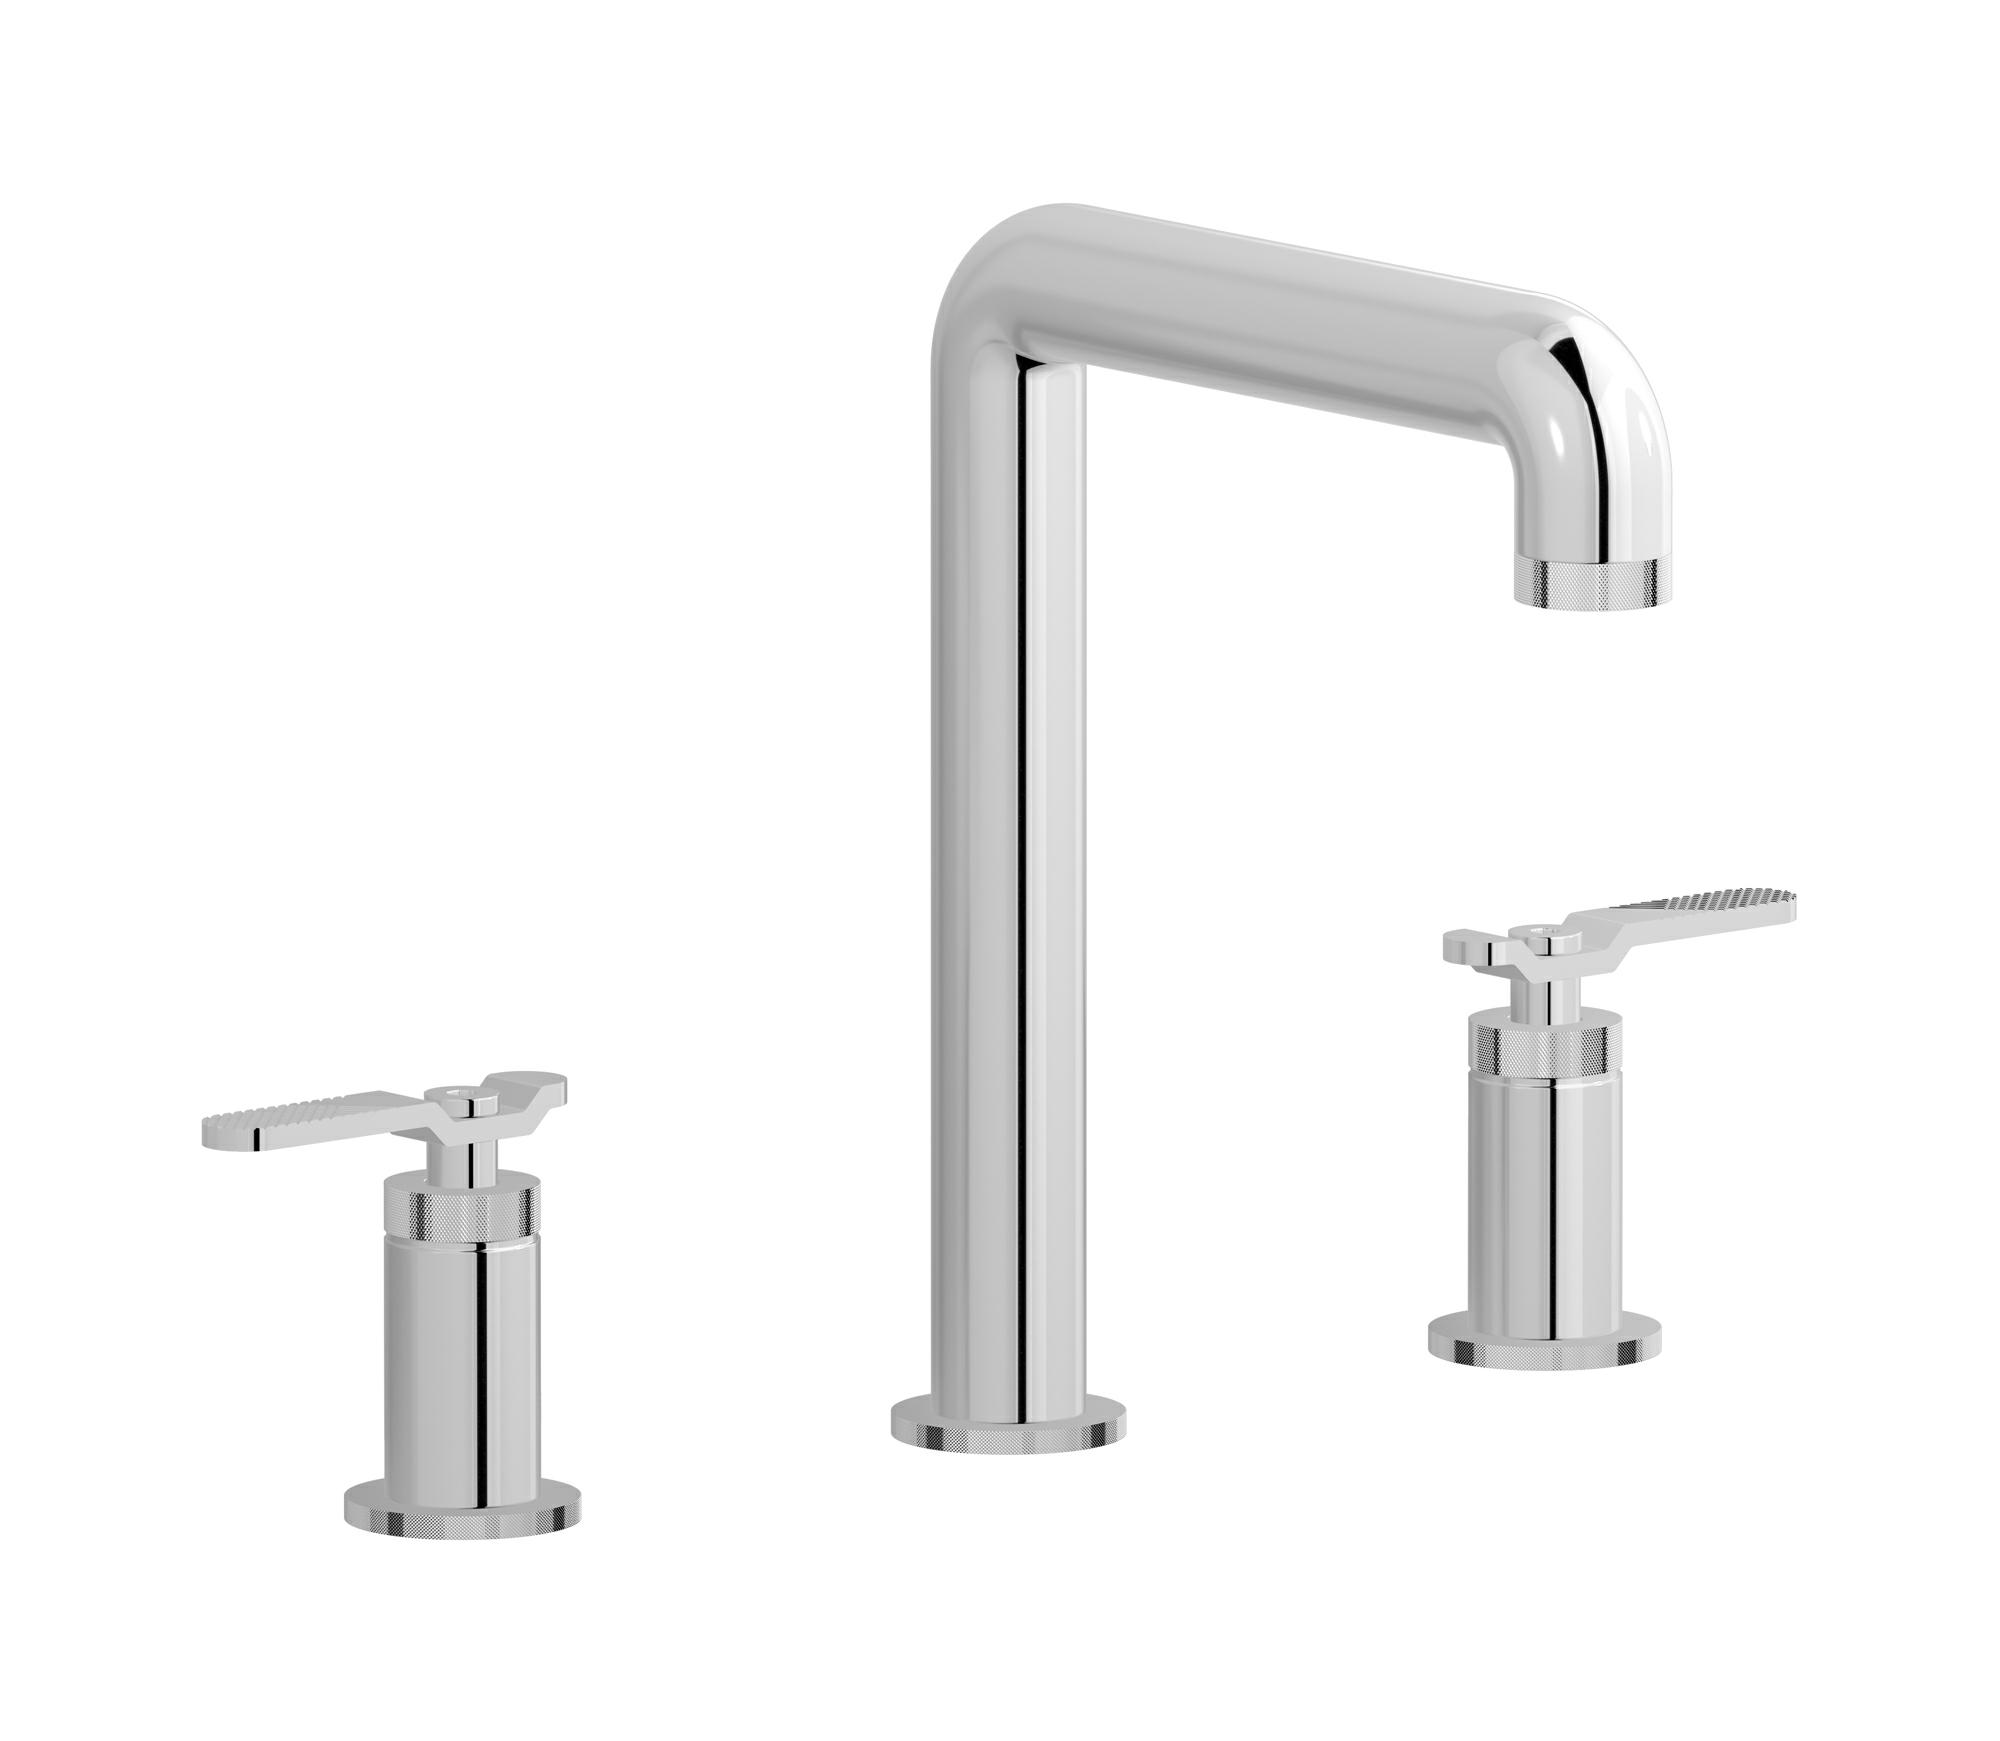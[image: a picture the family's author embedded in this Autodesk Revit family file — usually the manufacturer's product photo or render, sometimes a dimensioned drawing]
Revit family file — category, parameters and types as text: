
# Revit family: B2390
name_source: partatom
category: Apparecchi idraulici
units: mm (PartAtom-declared; Revit-internal decimal feet)

## family parameters
Basato su piano di lavoro = No
Condiviso = No
Mantieni orientamento annotazione = No
Numero OmniClass = 23.45.55.17
Punto di calcolo locali = No
Quota connettore circolare = Usa diametro
Sempre verticale = Sì
Taglio con vuoti quando caricato = No
Tipo di parte = Normale
Titolo OmniClass = Mixing Faucets

## types (13) — shared parameters
Cold water inlet = 10 mm  [stored 0.0328084 ft]
Commenti sul tipo = Three holes washbasin set with tall spout
Connessione CW = No
Connessione HW = No
Connessione di scarico = No
Connessione di ventilazione = No
Descrizione = Three holes washbasin set with tall spout
Hot water inlet = 10 mm  [stored 0.0328084 ft]
Produttore = IB Rubinetterie S.p.A.
URL = https://www.weareib.it
zero-valued in all types: Prospetto di default

## per-type parameters (varying)
| type | Finishes surface | Immagine tipo | Modello |
| Chrome | IB_Chrome | B2390CC.jpg | B2390CC |
| Black Chrome | IB_Black chrome | B2390CF.jpg | B2390CF |
| Brushed Black Chrome | IB_Brushed black chrome | B2390CS.jpg | B2390CS |
| Pale Gold | IB_Pale gold | B2390II.jpg | B2390II |
| Brushed Pale Gold | IB_brushed pale gold | B2390IS.jpg | B2390IS |
| Matt Black | IB_matt black | B2390NP.jpg | B2390NP |
| Natural Brass | IB_Brass | B2390ON.jpg | B2390ON |
| Gold | IB_gold | B2390OO.jpg | B2390OO |
| Brushed Gold | IB_brushed gold | B2390OS.jpg | B2390OS |
| Rose Gold | IB_Rose gold | B2390RS.jpg | B2390RS |
| Brushed Rose Gold | IB_Brushed rose gold | B2390SR.jpg | B2390SR |
| Brushed Nickel | IB_Brushed nickel | B2390SS.jpg | B2390SS |
| Modern Bronze | IB_Modern bronze | B2390MB.jpg | B2390MB |

note: [stored X ft] marks values corroborated as IEEE doubles in the binary element streams (Revit-internal decimal feet)
